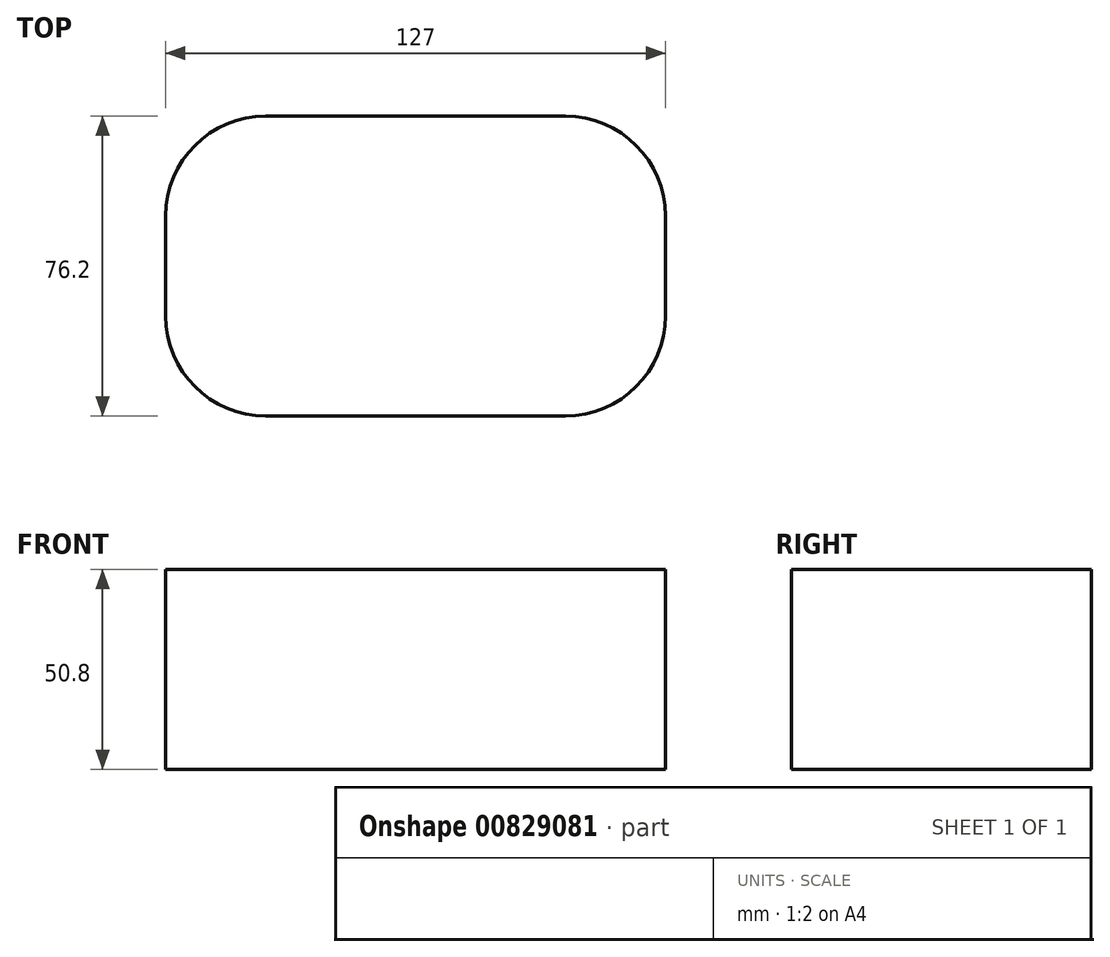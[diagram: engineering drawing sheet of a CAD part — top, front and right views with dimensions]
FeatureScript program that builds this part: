
annotation { "Feature Type Name" : "Feature", "Feature Type Description" : "" }
export const myFeature = defineFeature(function(context is Context, id is Id, definition is map)
    precondition{}
    {
        {
            var Q0;
            Q0=qCreatedBy(makeId("Top.planeOp"),FACE);
            var sketch = newSketch(context, id + "F0", { "sketchPlane" : qUnion([Q0])});
            skLineSegment(sketch, "E0.bottom", {"start": v(63.5, 38.1) * mm, "end": v(-63.5, 38.1) * mm});
            skLineSegment(sketch, "E0.top", {"start": v(63.5, -38.1) * mm, "end": v(-63.5, -38.1) * mm});
            skLineSegment(sketch, "E0.left", {"start": v(63.5, 38.1) * mm, "end": v(63.5, -38.1) * mm});
            skLineSegment(sketch, "E0.right", {"start": v(-63.5, 38.1) * mm, "end": v(-63.5, -38.1) * mm});
            skPoint(sketch, "E0.middle", {"position": v(0, 0) * mm});
            skSolve(sketch);
        }
        {
            var Q0;
            Q0=makeQuery(id+"F0.imprint","IMPRINT",FACE,{"disambiguationData":[TD([[makeQuery(id+"F0.imprint","IMPRINT",EDGE,{"derivedFrom":sQuery(id+"F0.wireOp",EDGE,"E0.bottom")}),1.0]])]});
            extrude(context, id + "F1", {"entities" : qUnion([Q0]), "depth" : 50.8 * mm, "offsetDistance" : 25.4 * mm});
        }
        {
            var Q0;
            Q0=makeQuery(id+"F1.opExtrude","SWEPT_EDGE",EDGE,{"disambiguationData":[OSD([sQuery(id+"F0.wireOp",EDGE,"E0.top"),sQuery(id+"F0.wireOp",EDGE,"E0.left")])]});
            var Q1;
            Q1=makeQuery(id+"F1.opExtrude","SWEPT_EDGE",EDGE,{"disambiguationData":[OSD([sQuery(id+"F0.wireOp",EDGE,"E0.bottom"),sQuery(id+"F0.wireOp",EDGE,"E0.left")])]});
            var Q2;
            Q2=makeQuery(id+"F1.opExtrude","SWEPT_EDGE",EDGE,{"disambiguationData":[OSD([sQuery(id+"F0.wireOp",EDGE,"E0.top"),sQuery(id+"F0.wireOp",EDGE,"E0.right")])]});
            var Q3;
            Q3=makeQuery(id+"F1.opExtrude","SWEPT_EDGE",EDGE,{"disambiguationData":[OSD([sQuery(id+"F0.wireOp",EDGE,"E0.bottom"),sQuery(id+"F0.wireOp",EDGE,"E0.right")])]});
            fillet(context, id + "F2", {"entities" : qUnion([Q0, Q1, Q2, Q3]), "tangentPropagation" : true, "radius" : 25.4 * mm, "defaultsChanged" : false, "vertexSettings" : [], "allowEdgeOverflow" : false});
        }
    });
